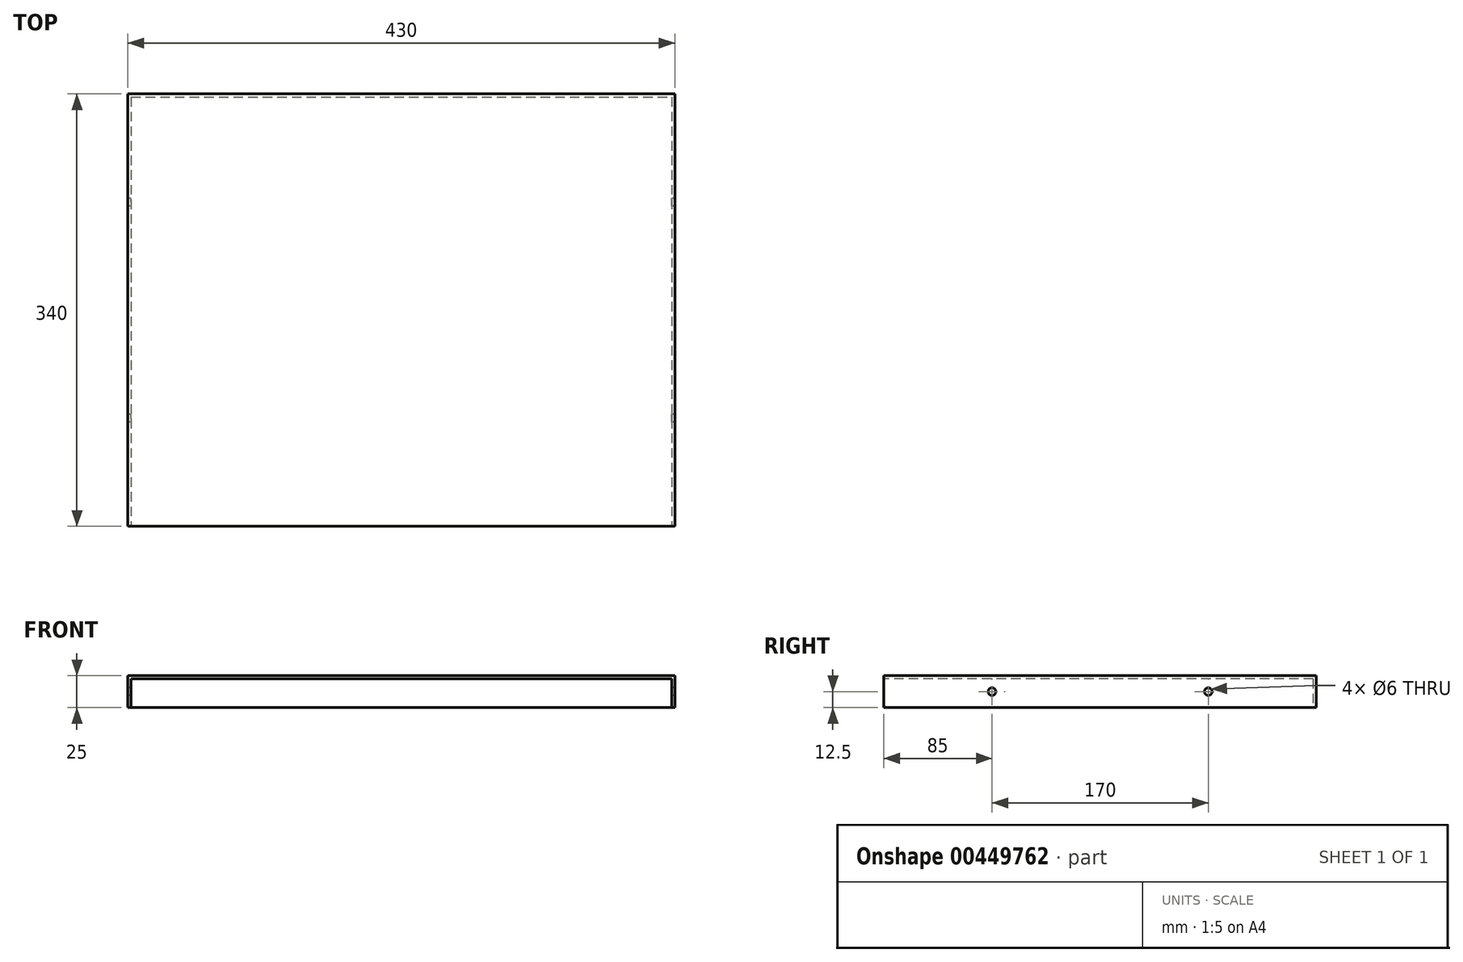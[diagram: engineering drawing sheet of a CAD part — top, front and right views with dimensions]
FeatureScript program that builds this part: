
annotation { "Feature Type Name" : "Feature", "Feature Type Description" : "" }
export const myFeature = defineFeature(function(context is Context, id is Id, definition is map)
    precondition{}
    {
        {
            var Q0;
            Q0=qCreatedBy(makeId("Top.planeOp"),FACE);
            var sketch = newSketch(context, id + "F0", { "sketchPlane" : qUnion([Q0])});
            skLineSegment(sketch, "E0.bottom", {"start": v(-215, 170) * mm, "end": v(215, 170) * mm});
            skLineSegment(sketch, "E0.top", {"start": v(-215, -170) * mm, "end": v(215, -170) * mm});
            skLineSegment(sketch, "E0.left", {"start": v(-215, 170) * mm, "end": v(-215, -170) * mm});
            skLineSegment(sketch, "E0.right", {"start": v(215, 170) * mm, "end": v(215, -170) * mm});
            skPoint(sketch, "E0.middle", {"position": v(0, 0) * mm});
            skSolve(sketch);
        }
        {
            var Q0;
            Q0=makeQuery(id+"F0.imprint","IMPRINT",FACE,{"disambiguationData":[TD([[makeQuery(id+"F0.imprint","IMPRINT",EDGE,{"derivedFrom":sQuery(id+"F0.wireOp",EDGE,"E0.bottom")}),-1.0]])]});
            extrude(context, id + "F1", {"entities" : qUnion([Q0]), "depth" : 25 * mm});
        }
        {
            var Q0;
            Q0=makeQuery(id+"F1.opExtrude","CAP_FACE",FACE,{"disambiguationData":[OSD([sQuery(id+"F0.wireOp",EDGE,"E0.bottom"),sQuery(id+"F0.wireOp",EDGE,"E0.top"),sQuery(id+"F0.wireOp",EDGE,"E0.left"),sQuery(id+"F0.wireOp",EDGE,"E0.right")])],"isStart":true});
            var Q1;
            Q1=makeQuery(id+"F1.opExtrude","SWEPT_FACE",FACE,{"disambiguationData":[OSD([sQuery(id+"F0.wireOp",EDGE,"E0.top")])]});
            shell(context, id + "F2", {"entities" : qUnion([Q0, Q1]), "thickness" : 2.5 * mm});
        }
        {
            var Q0;
            Q0=makeQuery(id+"F1.opExtrude","SWEPT_FACE",FACE,{"disambiguationData":[OSD([sQuery(id+"F0.wireOp",EDGE,"E0.left")])]});
            var sketch = newSketch(context, id + "F3", { "sketchPlane" : qUnion([Q0])});
            skPoint(sketch, "E1", {"position": v(-170, 12.5) * mm});
            skPoint(sketch, "E2", {"position": v(170, 12.5) * mm});
            skPoint(sketch, "E3", {"position": v(0, 25) * mm});
            skPoint(sketch, "E4", {"position": v(0, 12.5) * mm});
            skPoint(sketch, "E5", {"position": v(85, 12.5) * mm});
            skPoint(sketch, "E6", {"position": v(-85, 12.5) * mm});
            skSolve(sketch);
        }
        {
            var Q0;
            Q0=sQuery(id+"F3.wireOp",VERTEX,"E6");
            var Q1;
            Q1=sQuery(id+"F3.wireOp",VERTEX,"E5");
            var Q2;
            Q2=makeQuery(id+"F1.opExtrude","SWEPT_BODY",BODY,{"disambiguationData":[OSD([sQuery(id+"F0.wireOp",EDGE,"E0.bottom"),sQuery(id+"F0.wireOp",EDGE,"E0.top"),sQuery(id+"F0.wireOp",EDGE,"E0.left"),sQuery(id+"F0.wireOp",EDGE,"E0.right")])]});
            hole(context, id + "F4", {"style" : HoleStyle.C_BORE, "endStyle" : HoleEndStyle.BLIND, "holeDiameter" : 6 * mm, "cBoreDiameter" : 6 * mm, "cBoreDepth" : 5 * mm, "holeDepth" : 1000 * mm, "isTappedThrough" : true, "tappedDepth" : 12 * mm, "tapClearance" : 3, "startFromSketch" : true, "locations" : qUnion([Q0, Q1]), "scope" : qUnion([Q2])});
        }
    });
